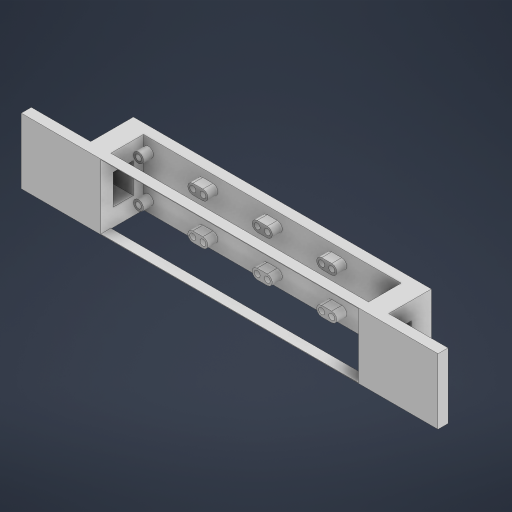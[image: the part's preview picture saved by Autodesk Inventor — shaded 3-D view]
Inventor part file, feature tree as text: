
AUTODESK INVENTOR PART (.ipt)
format: ipt  version: 2024.2 (Build 282272000, 272)  size: 680,960 bytes
history: native  units: mm
features: extrude x7, sketch x6, other x4, projected_geometry x3, reference x2
ambient origin geometry x8: Origin, YZ Plane, XZ Plane, XY Plane, X Axis, Y Axis, Z Axis, Center Point
bodies: Body1 (feature_tree)
feature tree (22):
  other  "솔리드1"
  extrude  "돌출1"  Depth=5.0mm TaperAngle=0.0deg
  extrude  "돌출2"  Depth=128.0mm
  extrude  "돌출3"  Depth=32.0mm
  extrude  "돌출4"  Depth=207.0mm
  sketch  "스케치5"
  extrude  "돌출5"  Depth=103.5mm
  extrude  "돌출6"  Depth=32.526912mm
  extrude  "돌출7"  Depth=5.0mm TaperAngle=0.0deg
  sketch  "스케치1"
  reference  "참조1"
  reference  "참조2"
  sketch  "스케치2"
  projected_geometry  "투영된 루프1"
  sketch  "스케치3"
  sketch  "스케치4"
  projected_geometry  "투영된 루프2"
  sketch  "스케치7"
  projected_geometry  "투영된 루프3"
  other  "<userpath>\Downloads\AAST\PART\AAST Remote Controler\AASTRC case.iam"
  other  "AASTRC case.iam"
  other  "AASTRC Bottom case:1"
